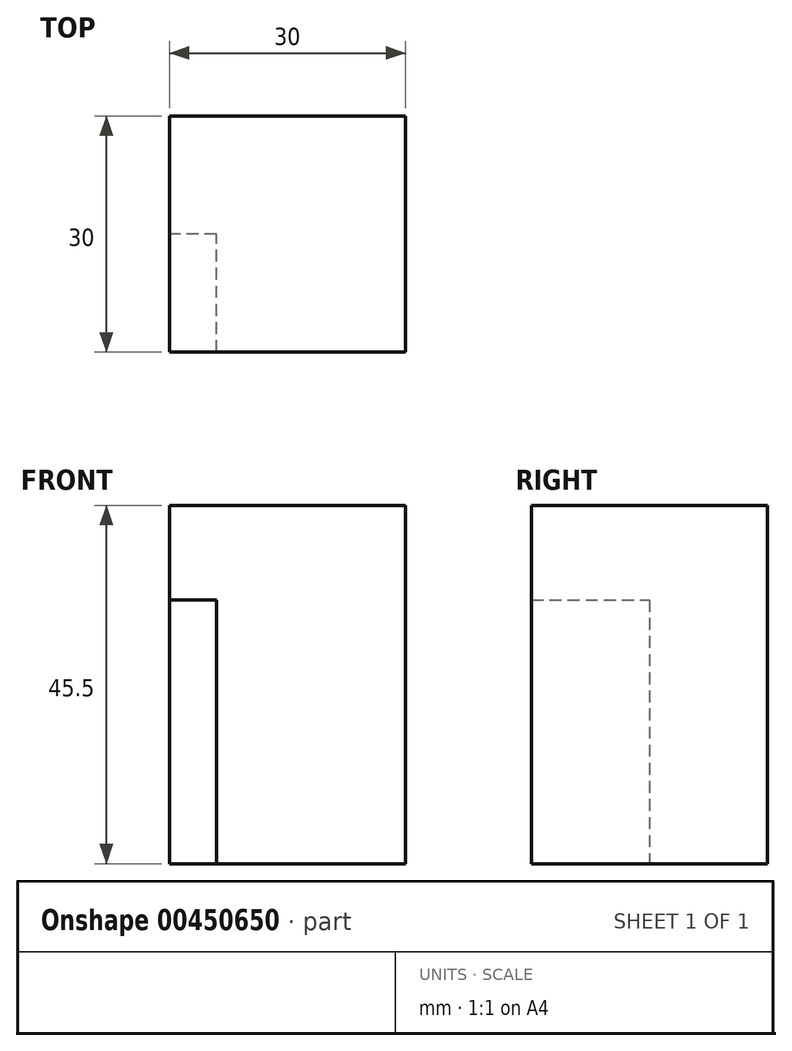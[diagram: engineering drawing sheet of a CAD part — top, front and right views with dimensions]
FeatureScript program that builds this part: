
annotation { "Feature Type Name" : "Feature", "Feature Type Description" : "" }
export const myFeature = defineFeature(function(context is Context, id is Id, definition is map)
    precondition{}
    {
        {
            var Q0;
            Q0=qCreatedBy(makeId("Top.planeOp"),FACE);
            var sketch = newSketch(context, id + "F0", { "sketchPlane" : qUnion([Q0])});
            skLineSegment(sketch, "E0.bottom", {"start": v(15, -15) * mm, "end": v(-15, -15) * mm});
            skLineSegment(sketch, "E0.top", {"start": v(15, 15) * mm, "end": v(-15, 15) * mm});
            skLineSegment(sketch, "E0.left", {"start": v(15, -15) * mm, "end": v(15, 15) * mm});
            skLineSegment(sketch, "E0.right", {"start": v(-15, -15) * mm, "end": v(-15, 15) * mm});
            skPoint(sketch, "E0.middle", {"position": v(0, 0) * mm});
            skSolve(sketch);
        }
        {
            var Q0;
            Q0=makeQuery(id+"F0.imprint","IMPRINT",FACE,{"disambiguationData":[TD([[makeQuery(id+"F0.imprint","IMPRINT",EDGE,{"derivedFrom":sQuery(id+"F0.wireOp",EDGE,"E0.bottom")}),-1.0]])]});
            extrude(context, id + "F1", {"entities" : qUnion([Q0]), "depth" : 45.5 * mm});
        }
        {
            var Q0;
            Q0=makeQuery(id+"F1.opExtrude","SWEPT_FACE",FACE,{"disambiguationData":[OSD([sQuery(id+"F0.wireOp",EDGE,"E0.right")])]});
            var sketch = newSketch(context, id + "F2", { "sketchPlane" : qUnion([Q0])});
            skLineSegment(sketch, "E1.bottom", {"start": v(15, 33.5) * mm, "end": v(0, 33.5) * mm});
            skLineSegment(sketch, "E1.top", {"start": v(15, 0) * mm, "end": v(0, 0) * mm});
            skLineSegment(sketch, "E1.left", {"start": v(15, 33.5) * mm, "end": v(15, 0) * mm});
            skLineSegment(sketch, "E1.right", {"start": v(0, 33.5) * mm, "end": v(0, 0) * mm});
            skSolve(sketch);
        }
        {
            var Q0;
            Q0=makeQuery(id+"F2.imprint","IMPRINT",FACE,{"disambiguationData":[TD([[makeQuery(id+"F2.imprint","IMPRINT",EDGE,{"derivedFrom":sQuery(id+"F2.wireOp",EDGE,"E1.bottom")}),1.0]])]});
            extrude(context, id + "F3", {"entities" : qUnion([Q0]), "operationType" : NewBodyOperationType.REMOVE, "oppositeDirection" : true, "depth" : 6 * mm});
        }
    });
